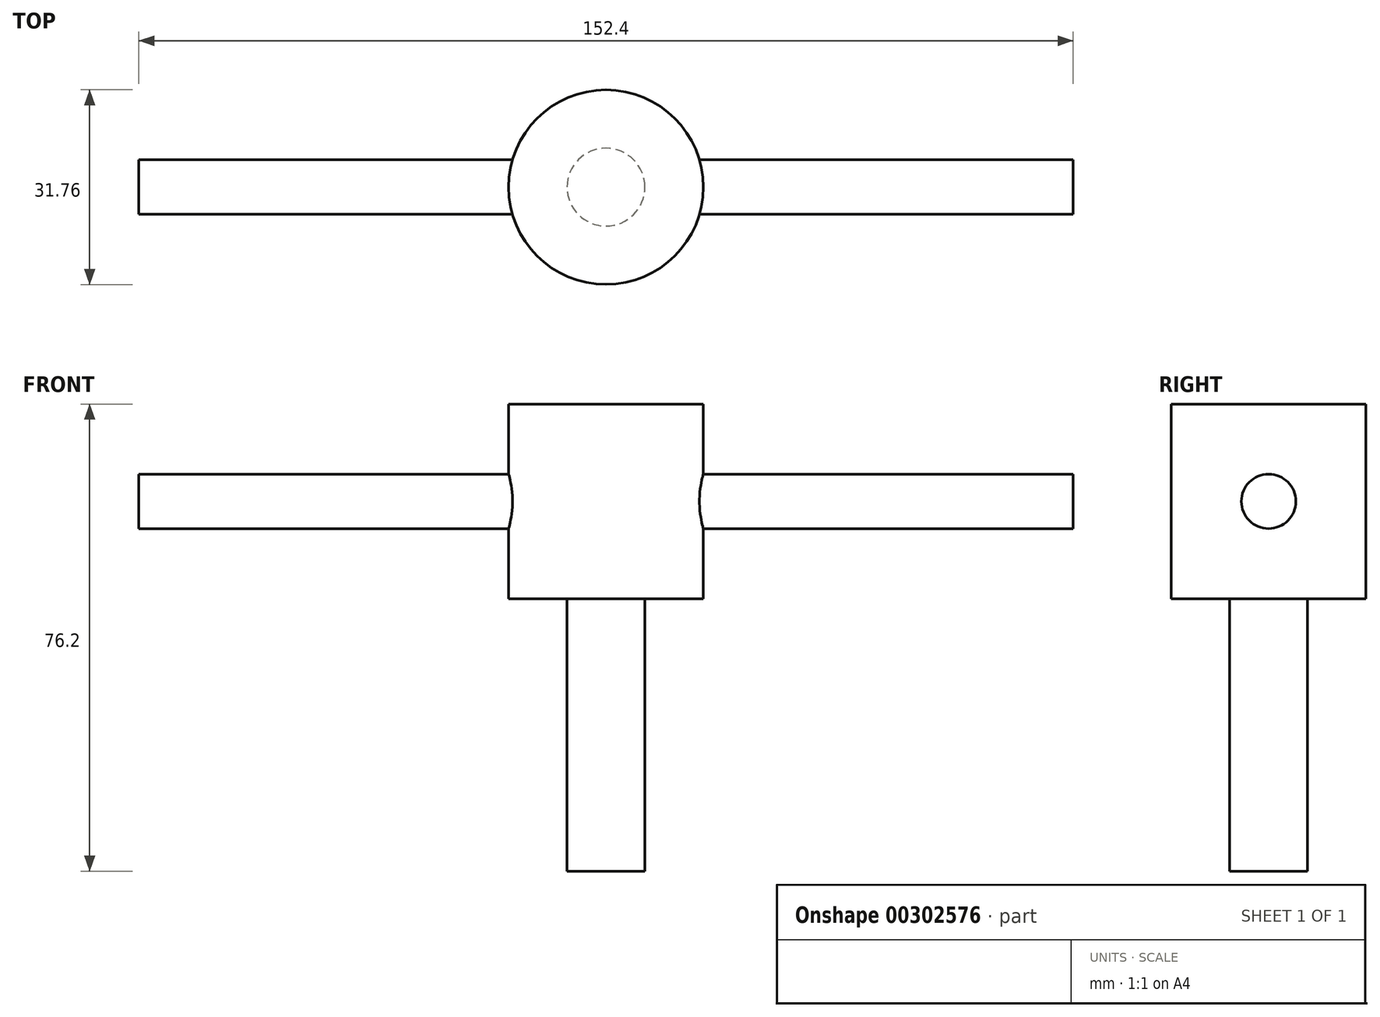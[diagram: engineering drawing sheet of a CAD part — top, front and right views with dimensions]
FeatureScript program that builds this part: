
annotation { "Feature Type Name" : "Feature", "Feature Type Description" : "" }
export const myFeature = defineFeature(function(context is Context, id is Id, definition is map)
    precondition{}
    {
        {
            var Q0;
            Q0=qCreatedBy(makeId("Top.planeOp"),FACE);
            var sketch = newSketch(context, id + "F0", { "sketchPlane" : qUnion([Q0])});
            skCircle(sketch, "E0", {"center": v(0, 0) * mm, "radius": 15.88 * mm});
            skSolve(sketch);
        }
        {
            var Q0;
            Q0 = qSketchRegion(id + "F0", true);
            extrude(context, id + "F1", {"entities" : qUnion([Q0]), "depth" : 31.75 * mm});
        }
        {
            var Q0;
            Q0=makeQuery(id+"F1.opExtrude","CAP_FACE",FACE,{"disambiguationData":[OSD([sQuery(id+"F0.wireOp",EDGE,"E0")])],"isStart":true});
            var sketch = newSketch(context, id + "F2", { "sketchPlane" : qUnion([Q0])});
            skCircle(sketch, "E1", {"center": v(0, 0) * mm, "radius": 6.35 * mm});
            skSolve(sketch);
        }
        {
            var Q0;
            Q0 = qSketchRegion(id + "F2", true);
            extrude(context, id + "F3", {"entities" : qUnion([Q0]), "operationType" : NewBodyOperationType.ADD, "depth" : 44.45 * mm});
        }
        {
            var Q0;
            Q0=qCreatedBy(makeId("Right.planeOp"),FACE);
            var sketch = newSketch(context, id + "F4", { "sketchPlane" : qUnion([Q0])});
            skCircle(sketch, "E2", {"center": v(0, 15.88) * mm, "radius": 4.45 * mm});
            skSolve(sketch);
        }
        {
            var Q0;
            Q0 = qSketchRegion(id + "F4", true);
            extrude(context, id + "F5", {"entities" : qUnion([Q0]), "operationType" : NewBodyOperationType.ADD, "depth" : 76.2 * mm, "hasSecondDirection" : true, "secondDirectionOppositeDirection" : true, "secondDirectionDepth" : 76.2 * mm});
        }
    });
